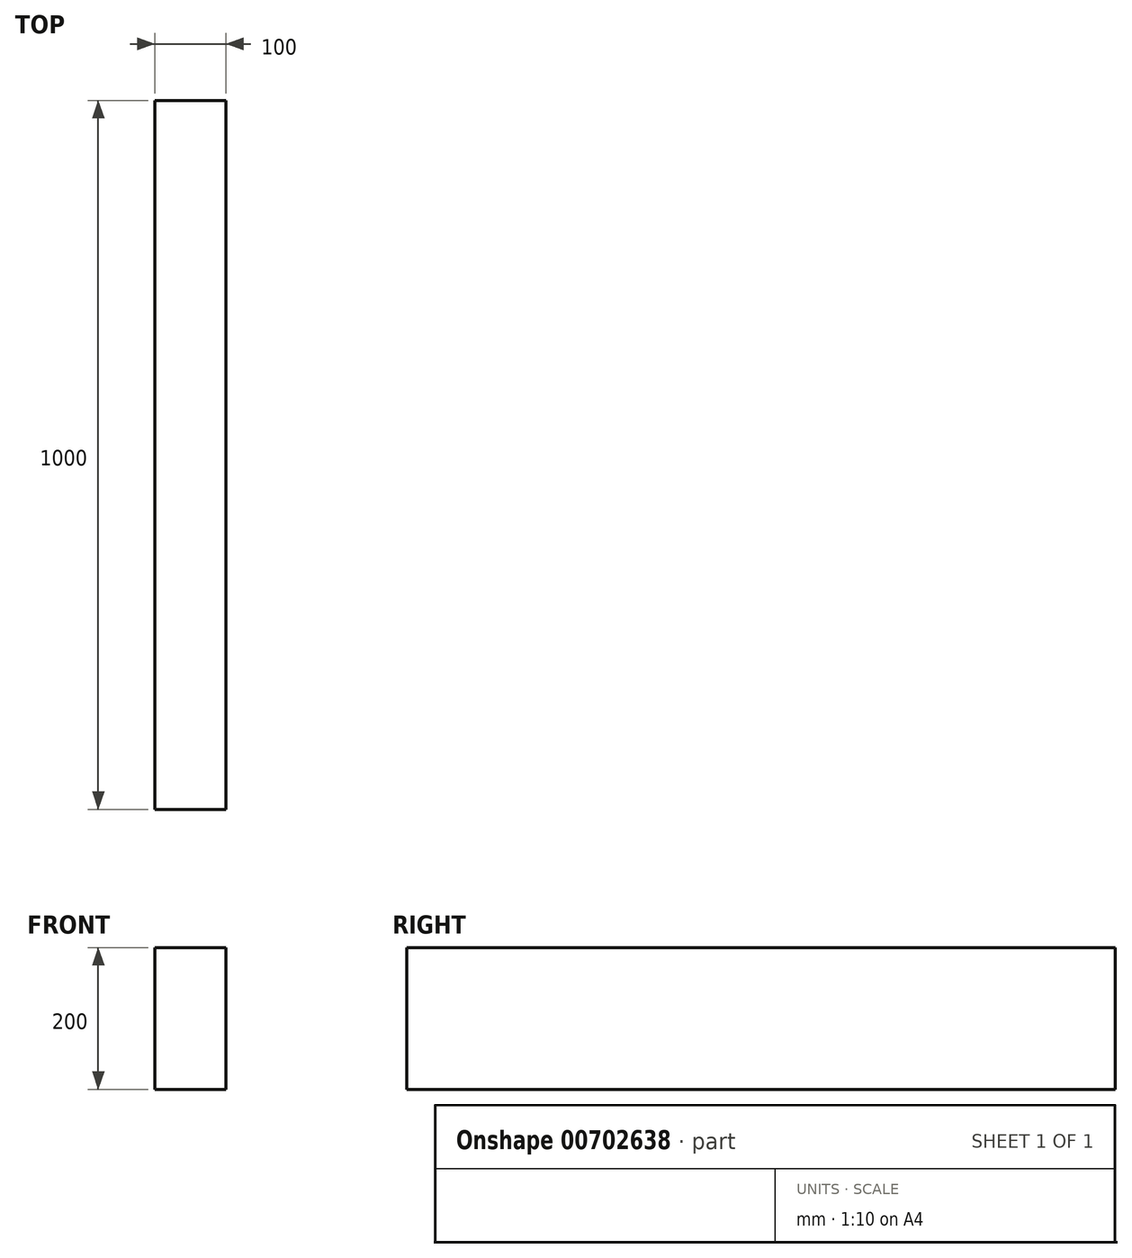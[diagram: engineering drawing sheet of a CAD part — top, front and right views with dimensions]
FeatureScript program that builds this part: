
annotation { "Feature Type Name" : "Feature", "Feature Type Description" : "" }
export const myFeature = defineFeature(function(context is Context, id is Id, definition is map)
    precondition{}
    {
        {
            var Q0;
            Q0=qCreatedBy(makeId("Front.planeOp"),FACE);
            var sketch = newSketch(context, id + "F0", { "sketchPlane" : qUnion([Q0])});
            skLineSegment(sketch, "E0.bottom", {"start": v(0, 0) * mm, "end": v(-100, 0) * mm});
            skLineSegment(sketch, "E0.top", {"start": v(0, 200) * mm, "end": v(-100, 200) * mm});
            skLineSegment(sketch, "E0.left", {"start": v(0, 0) * mm, "end": v(0, 200) * mm});
            skLineSegment(sketch, "E0.right", {"start": v(-100, 0) * mm, "end": v(-100, 200) * mm});
            skSolve(sketch);
        }
        {
            var Q0;
            Q0=qSketchRegion(id+"F0",true);
            extrude(context, id + "F1", {"entities" : qUnion([Q0]), "depth" : 1000 * mm, "offsetDistance" : 25 * mm});
        }
    });
